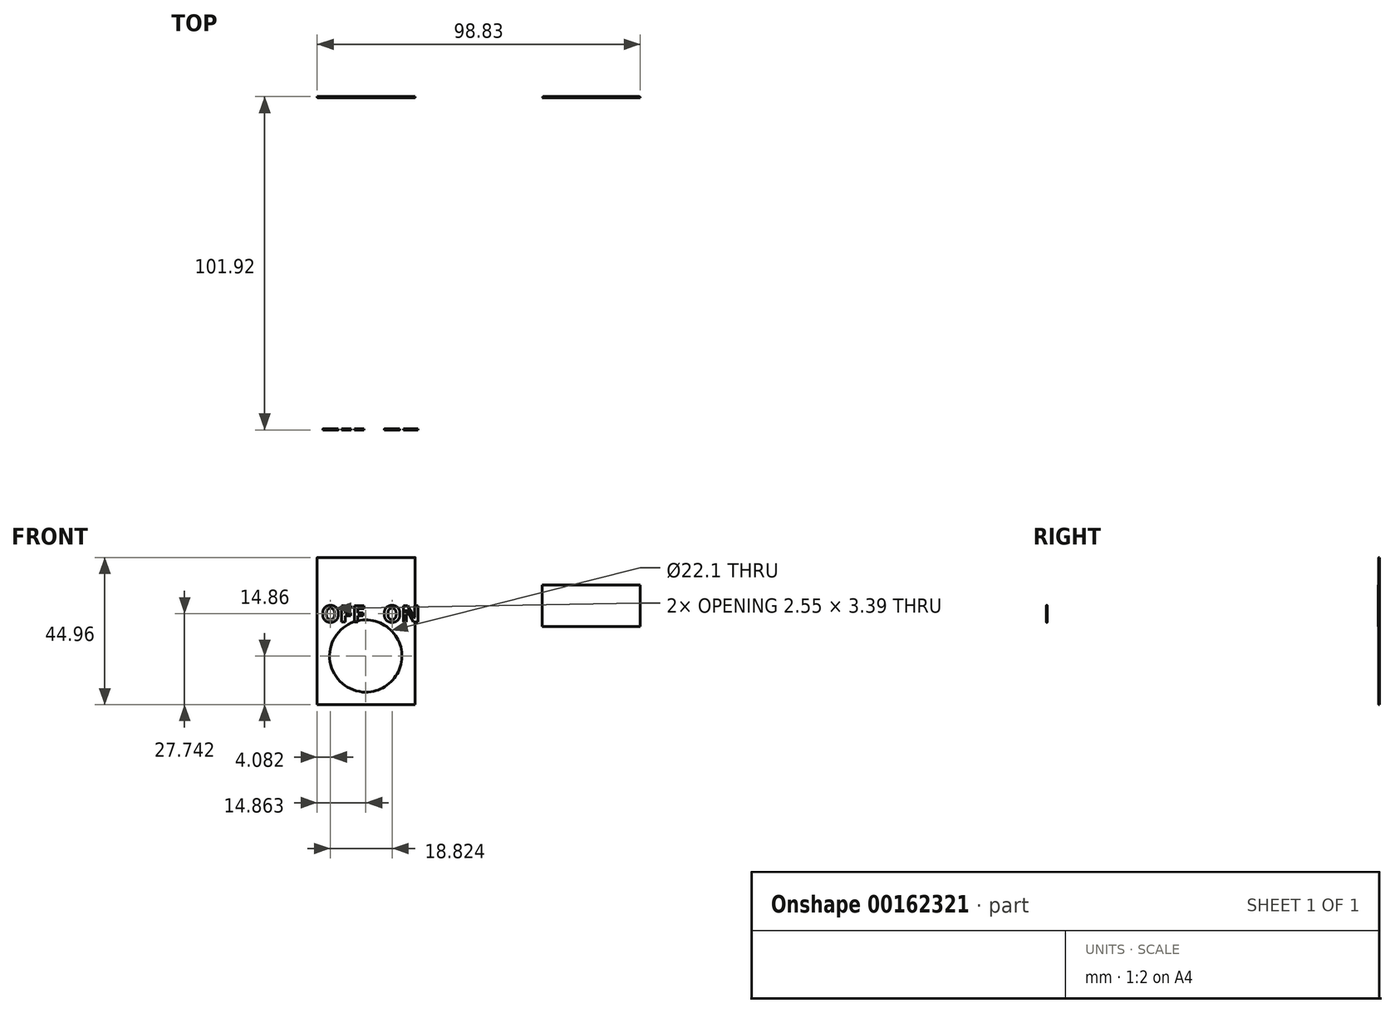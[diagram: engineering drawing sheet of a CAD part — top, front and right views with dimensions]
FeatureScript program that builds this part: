
annotation { "Feature Type Name" : "Feature", "Feature Type Description" : "" }
export const myFeature = defineFeature(function(context is Context, id is Id, definition is map)
    precondition{}
    {
        {
            var Q0;
            Q0=qCreatedBy(makeId("Front.planeOp"),FACE);
            var sketch = newSketch(context, id + "F0", { "sketchPlane" : qUnion([Q0])});
            skLineSegment(sketch, "E0.bottom", {"start": v(14.99, 22.48) * mm, "end": v(-14.99, 22.48) * mm});
            skLineSegment(sketch, "E0.top", {"start": v(14.99, -22.48) * mm, "end": v(-14.99, -22.48) * mm});
            skLineSegment(sketch, "E0.left", {"start": v(14.99, 22.48) * mm, "end": v(14.99, -22.48) * mm});
            skLineSegment(sketch, "E0.right", {"start": v(-14.99, 22.48) * mm, "end": v(-14.99, -22.48) * mm});
            skPoint(sketch, "E0.middle", {"position": v(0, 0) * mm});
            skCircle(sketch, "E1", {"center": v(-0.13, -7.62) * mm, "radius": 11.05 * mm});
            skSolve(sketch);
        }
        {
            var Q0;
            Q0 = qSketchRegion(id + "F0", true);
            extrude(context, id + "F1", {"entities" : qUnion([Q0]), "depth" : 0.32 * mm});
        }
        {
            var Q0;
            Q0=makeQuery(id+"F1.opExtrude","CAP_EDGE",EDGE,{"disambiguationData":[OSD([sQuery(id+"F0.wireOp",EDGE,"E0.right")])],"isStart":false});
            var Q1;
            Q1=makeQuery(id+"F1.opExtrude","CAP_EDGE",EDGE,{"disambiguationData":[OSD([sQuery(id+"F0.wireOp",EDGE,"E0.bottom")])],"isStart":false});
            var Q2;
            Q2=makeQuery(id+"F1.opExtrude","CAP_EDGE",EDGE,{"disambiguationData":[OSD([sQuery(id+"F0.wireOp",EDGE,"E0.left")])],"isStart":false});
            var Q3;
            Q3=makeQuery(id+"F1.opExtrude","CAP_EDGE",EDGE,{"disambiguationData":[OSD([sQuery(id+"F0.wireOp",EDGE,"E0.top")])],"isStart":false});
            fillet(context, id + "F2", {"entities" : qUnion([Q0, Q1, Q2, Q3]), "radius" : 0.16 * mm, "tangentPropagation" : true, "allowEdgeOverflow" : false});
        }
        {
            var Q0;
            Q0=qCreatedBy(makeId("Front.planeOp"),FACE);
            var sketch = newSketch(context, id + "F3", { "sketchPlane" : qUnion([Q0])});
            skText(sketch, "E2", { "text": "OFF   ON", "fontName": "OpenSans-Bold.ttf"});
            const initialGuessF3  = {"E2": [0.04344, 0.00274, 1, 0, 0.00507]};
            skSetInitialGuess(sketch, initialGuessF3);
            skSolve(sketch);
        }
        {
            var Q0;
            Q0=makeQuery(id+"F3.imprint","IMPRINT",FACE,{"disambiguationData":[TD([[makeQuery(id+"F3.imprint","IMPRINT",EDGE,{"derivedFrom":sQuery(id+"F3.wireOp",EDGE,"E2.sketch_text.stroke-0")}),-1.0]])]});
            var Q1;
            Q1=makeQuery(id+"F3.imprint","IMPRINT",FACE,{"disambiguationData":[TD([[makeQuery(id+"F3.imprint","IMPRINT",EDGE,{"derivedFrom":sQuery(id+"F3.wireOp",EDGE,"E2.sketch_text.stroke-14")}),-1.0]])]});
            var Q2;
            Q2=makeQuery(id+"F3.imprint","IMPRINT",FACE,{"disambiguationData":[TD([[makeQuery(id+"F3.imprint","IMPRINT",EDGE,{"derivedFrom":sQuery(id+"F3.wireOp",EDGE,"E2.sketch_text.stroke-24")}),-1.0]])]});
            var Q3;
            Q3=makeQuery(id+"F3.imprint","IMPRINT",FACE,{"disambiguationData":[TD([[makeQuery(id+"F3.imprint","IMPRINT",EDGE,{"derivedFrom":sQuery(id+"F3.wireOp",EDGE,"E2.sketch_text.stroke-34")}),-1.0]])]});
            var Q4;
            Q4=makeQuery(id+"F3.imprint","IMPRINT",FACE,{"disambiguationData":[TD([[makeQuery(id+"F3.imprint","IMPRINT",EDGE,{"derivedFrom":sQuery(id+"F3.wireOp",EDGE,"E2.sketch_text.stroke-48")}),-1.0]])]});
            extrude(context, id + "F4", {"entities" : qUnion([Q0, Q1, Q2, Q3, Q4]), "depth" : 0.32 * mm});
        }
        {
            var Q0;
            Q0=makeQuery(id+"F4.opExtrude","SWEPT_BODY",BODY,{"disambiguationData":[OSD([sQuery(id+"F3.wireOp",EDGE,"E2.sketch_text.stroke-0"),sQuery(id+"F3.wireOp",EDGE,"E2.sketch_text.stroke-1"),sQuery(id+"F3.wireOp",EDGE,"E2.sketch_text.stroke-2"),sQuery(id+"F3.wireOp",EDGE,"E2.sketch_text.stroke-3"),sQuery(id+"F3.wireOp",EDGE,"E2.sketch_text.stroke-4"),sQuery(id+"F3.wireOp",EDGE,"E2.sketch_text.stroke-5"),sQuery(id+"F3.wireOp",EDGE,"E2.sketch_text.stroke-6"),sQuery(id+"F3.wireOp",EDGE,"E2.sketch_text.stroke-7"),sQuery(id+"F3.wireOp",EDGE,"E2.sketch_text.stroke-8"),sQuery(id+"F3.wireOp",EDGE,"E2.sketch_text.stroke-9"),sQuery(id+"F3.wireOp",EDGE,"E2.sketch_text.stroke-10"),sQuery(id+"F3.wireOp",EDGE,"E2.sketch_text.stroke-11"),sQuery(id+"F3.wireOp",EDGE,"E2.sketch_text.stroke-12"),sQuery(id+"F3.wireOp",EDGE,"E2.sketch_text.stroke-13")])]});
            var Q1;
            Q1=makeQuery(id+"F4.opExtrude","CAP_VERTEX",VERTEX,{"disambiguationData":[OSD([sQuery(id+"F3.wireOp",EDGE,"E2.sketch_text.stroke-10"),sQuery(id+"F3.wireOp",EDGE,"E2.sketch_text.stroke-11")])],"isStart":false});
            var Q2;
            Q2=makeQuery(id+"F4.opExtrude","CAP_VERTEX",VERTEX,{"disambiguationData":[OSD([sQuery(id+"F3.wireOp",EDGE,"E2.sketch_text.stroke-12"),sQuery(id+"F3.wireOp",EDGE,"E2.sketch_text.stroke-13")])],"isStart":false});
            transform(context, id + "F5", {"entities" : qUnion([Q0]), "transformType" : TransformType.TRANSLATION_3D, "dx" : -57.15 * mm, "dy" : -101.6 * mm, "dz" : 0 * mm, "makeCopy" : false});
        }
        {
            var Q0;
            Q0=makeQuery(id+"F4.opExtrude","SWEPT_BODY",BODY,{"disambiguationData":[OSD([sQuery(id+"F3.wireOp",EDGE,"E2.sketch_text.stroke-14"),sQuery(id+"F3.wireOp",EDGE,"E2.sketch_text.stroke-15"),sQuery(id+"F3.wireOp",EDGE,"E2.sketch_text.stroke-16"),sQuery(id+"F3.wireOp",EDGE,"E2.sketch_text.stroke-17"),sQuery(id+"F3.wireOp",EDGE,"E2.sketch_text.stroke-18"),sQuery(id+"F3.wireOp",EDGE,"E2.sketch_text.stroke-19"),sQuery(id+"F3.wireOp",EDGE,"E2.sketch_text.stroke-20"),sQuery(id+"F3.wireOp",EDGE,"E2.sketch_text.stroke-21"),sQuery(id+"F3.wireOp",EDGE,"E2.sketch_text.stroke-22"),sQuery(id+"F3.wireOp",EDGE,"E2.sketch_text.stroke-23")])]});
            transform(context, id + "F6", {"entities" : qUnion([Q0]), "transformType" : TransformType.TRANSLATION_3D, "dx" : -57.15 * mm, "dy" : -101.6 * mm, "dz" : 0 * mm, "makeCopy" : false});
        }
        {
            var Q0;
            Q0=makeQuery(id+"F4.opExtrude","SWEPT_BODY",BODY,{"disambiguationData":[OSD([sQuery(id+"F3.wireOp",EDGE,"E2.sketch_text.stroke-24"),sQuery(id+"F3.wireOp",EDGE,"E2.sketch_text.stroke-25"),sQuery(id+"F3.wireOp",EDGE,"E2.sketch_text.stroke-26"),sQuery(id+"F3.wireOp",EDGE,"E2.sketch_text.stroke-27"),sQuery(id+"F3.wireOp",EDGE,"E2.sketch_text.stroke-28"),sQuery(id+"F3.wireOp",EDGE,"E2.sketch_text.stroke-29"),sQuery(id+"F3.wireOp",EDGE,"E2.sketch_text.stroke-30"),sQuery(id+"F3.wireOp",EDGE,"E2.sketch_text.stroke-31"),sQuery(id+"F3.wireOp",EDGE,"E2.sketch_text.stroke-32"),sQuery(id+"F3.wireOp",EDGE,"E2.sketch_text.stroke-33")])]});
            transform(context, id + "F7", {"entities" : qUnion([Q0]), "transformType" : TransformType.TRANSLATION_3D, "dx" : -57.15 * mm, "dy" : -101.6 * mm, "dz" : 0 * mm, "makeCopy" : false});
        }
        {
            var Q0;
            Q0=makeQuery(id+"F4.opExtrude","SWEPT_BODY",BODY,{"disambiguationData":[OSD([sQuery(id+"F3.wireOp",EDGE,"E2.sketch_text.stroke-34"),sQuery(id+"F3.wireOp",EDGE,"E2.sketch_text.stroke-35"),sQuery(id+"F3.wireOp",EDGE,"E2.sketch_text.stroke-36"),sQuery(id+"F3.wireOp",EDGE,"E2.sketch_text.stroke-37"),sQuery(id+"F3.wireOp",EDGE,"E2.sketch_text.stroke-38"),sQuery(id+"F3.wireOp",EDGE,"E2.sketch_text.stroke-39"),sQuery(id+"F3.wireOp",EDGE,"E2.sketch_text.stroke-40"),sQuery(id+"F3.wireOp",EDGE,"E2.sketch_text.stroke-41"),sQuery(id+"F3.wireOp",EDGE,"E2.sketch_text.stroke-42"),sQuery(id+"F3.wireOp",EDGE,"E2.sketch_text.stroke-43"),sQuery(id+"F3.wireOp",EDGE,"E2.sketch_text.stroke-44"),sQuery(id+"F3.wireOp",EDGE,"E2.sketch_text.stroke-45"),sQuery(id+"F3.wireOp",EDGE,"E2.sketch_text.stroke-46"),sQuery(id+"F3.wireOp",EDGE,"E2.sketch_text.stroke-47")])]});
            transform(context, id + "F8", {"entities" : qUnion([Q0]), "transformType" : TransformType.TRANSLATION_3D, "dx" : -57.15 * mm, "dy" : -101.6 * mm, "dz" : 0 * mm, "makeCopy" : false});
        }
        {
            var Q0;
            Q0=makeQuery(id+"F4.opExtrude","SWEPT_BODY",BODY,{"disambiguationData":[OSD([sQuery(id+"F3.wireOp",EDGE,"E2.sketch_text.stroke-48"),sQuery(id+"F3.wireOp",EDGE,"E2.sketch_text.stroke-49"),sQuery(id+"F3.wireOp",EDGE,"E2.sketch_text.stroke-50"),sQuery(id+"F3.wireOp",EDGE,"E2.sketch_text.stroke-51"),sQuery(id+"F3.wireOp",EDGE,"E2.sketch_text.stroke-52"),sQuery(id+"F3.wireOp",EDGE,"E2.sketch_text.stroke-53"),sQuery(id+"F3.wireOp",EDGE,"E2.sketch_text.stroke-54"),sQuery(id+"F3.wireOp",EDGE,"E2.sketch_text.stroke-55"),sQuery(id+"F3.wireOp",EDGE,"E2.sketch_text.stroke-56"),sQuery(id+"F3.wireOp",EDGE,"E2.sketch_text.stroke-57"),sQuery(id+"F3.wireOp",EDGE,"E2.sketch_text.stroke-58"),sQuery(id+"F3.wireOp",EDGE,"E2.sketch_text.stroke-59"),sQuery(id+"F3.wireOp",EDGE,"E2.sketch_text.stroke-60"),sQuery(id+"F3.wireOp",EDGE,"E2.sketch_text.stroke-61")])]});
            transform(context, id + "F9", {"entities" : qUnion([Q0]), "transformType" : TransformType.TRANSLATION_3D, "dx" : -57.15 * mm, "dy" : -101.6 * mm, "dz" : 0 * mm, "makeCopy" : false});
        }
        {
            var Q0;
            Q0=qCreatedBy(makeId("Front.planeOp"),FACE);
            var sketch = newSketch(context, id + "F10", { "sketchPlane" : qUnion([Q0])});
            skLineSegment(sketch, "E3.bottom", {"start": v(53.87, 14.05) * mm, "end": v(83.84, 14.05) * mm});
            skLineSegment(sketch, "E3.top", {"start": v(53.87, 1.35) * mm, "end": v(83.84, 1.35) * mm});
            skLineSegment(sketch, "E3.left", {"start": v(53.87, 14.05) * mm, "end": v(53.87, 1.35) * mm});
            skLineSegment(sketch, "E3.right", {"start": v(83.84, 14.05) * mm, "end": v(83.84, 1.35) * mm});
            skSolve(sketch);
        }
        {
            var Q0;
            Q0 = qSketchRegion(id + "F10", true);
            extrude(context, id + "F11", {"entities" : qUnion([Q0]), "depth" : 0.38 * mm});
        }
        {
            var Q0;
            Q0=makeQuery(id+"F11.opExtrude","CAP_EDGE",EDGE,{"disambiguationData":[OSD([sQuery(id+"F10.wireOp",EDGE,"E3.bottom")])],"isStart":true});
            var Q1;
            Q1=makeQuery(id+"F11.opExtrude","CAP_EDGE",EDGE,{"disambiguationData":[OSD([sQuery(id+"F10.wireOp",EDGE,"E3.right")])],"isStart":true});
            var Q2;
            Q2=makeQuery(id+"F11.opExtrude","CAP_EDGE",EDGE,{"disambiguationData":[OSD([sQuery(id+"F10.wireOp",EDGE,"E3.top")])],"isStart":true});
            var Q3;
            Q3=makeQuery(id+"F11.opExtrude","CAP_EDGE",EDGE,{"disambiguationData":[OSD([sQuery(id+"F10.wireOp",EDGE,"E3.left")])],"isStart":true});
            fillet(context, id + "F12", {"entities" : qUnion([Q0, Q1, Q2, Q3]), "radius" : 0.38 * mm, "tangentPropagation" : true, "allowEdgeOverflow" : false});
        }
    });
